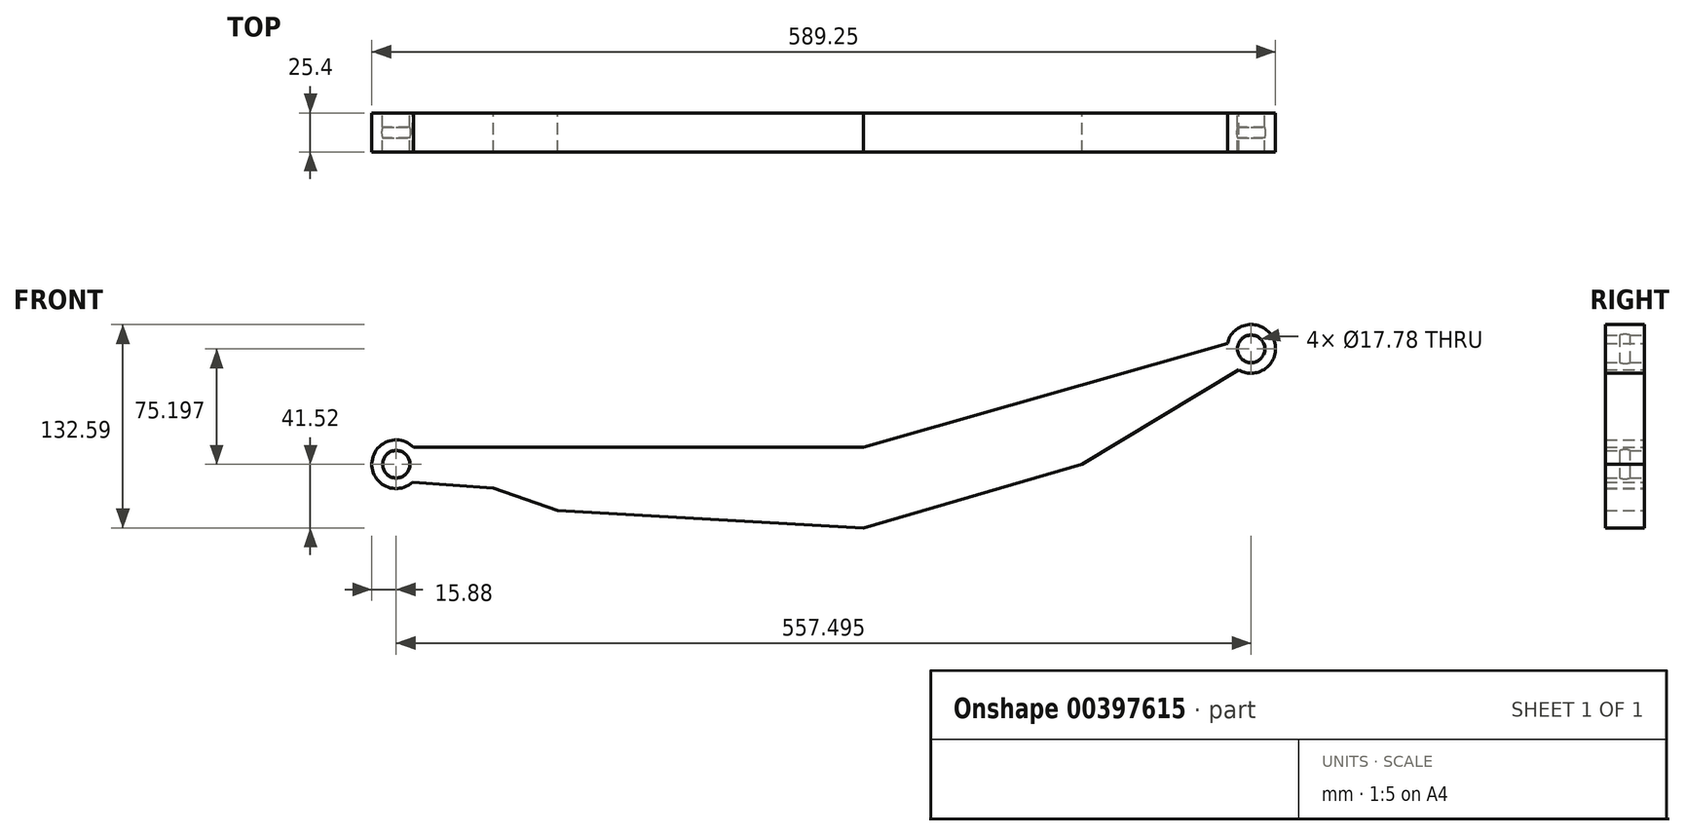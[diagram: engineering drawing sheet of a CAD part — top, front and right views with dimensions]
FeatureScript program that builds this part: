
annotation { "Feature Type Name" : "Feature", "Feature Type Description" : "" }
export const myFeature = defineFeature(function(context is Context, id is Id, definition is map)
    precondition{}
    {
        {
            var Q0;
            Q0=qCreatedBy(makeId("Front.planeOp"),FACE);
            var sketch = newSketch(context, id + "F0", { "sketchPlane" : qUnion([Q0])});
            skCircle(sketch, "E0", {"center": v(59.7, 0) * mm, "radius": 15.88 * mm});
            skLineSegment(sketch, "E1", {"start": v(59.7, 0) * mm, "end": v(59.7, 6.35) * mm});
            skLineSegment(sketch, "E2", {"start": v(59.7, 6.35) * mm, "end": v(59.7, 15.88) * mm});
            skLineSegment(sketch, "E3", {"start": v(59.7, 11.11) * mm, "end": v(364.5, 11.11) * mm});
            skLineSegment(sketch, "E4", {"start": v(59.7, 0) * mm, "end": v(59.7, -6.35) * mm});
            skLineSegment(sketch, "E5", {"start": v(59.7, -6.35) * mm, "end": v(59.7, -15.88) * mm});
            skLineSegment(sketch, "E6", {"start": v(59.7, -11.11) * mm, "end": v(123.05, -15.56) * mm});
            skLineSegment(sketch, "E7", {"start": v(123.05, -15.56) * mm, "end": v(164.98, -30.31) * mm});
            skLineSegment(sketch, "E8", {"start": v(164.98, -30.31) * mm, "end": v(364.5, -41.52) * mm});
            skLineSegment(sketch, "E9", {"start": v(364.5, -41.52) * mm, "end": v(364.5, 11.11) * mm});
            skLineSegment(sketch, "E10", {"start": v(614.5, 82.32) * mm, "end": v(619.92, 68.08) * mm});
            skCircle(sketch, "E11", {"center": v(617.2, 75.2) * mm, "radius": 15.88 * mm});
            skLineSegment(sketch, "E12", {"start": v(506.93, 0) * mm, "end": v(619.92, 68.08) * mm});
            skLineSegment(sketch, "E13", {"start": v(364.5, -41.52) * mm, "end": v(506.93, 0) * mm});
            skLineSegment(sketch, "E14", {"start": v(364.5, 11.11) * mm, "end": v(528.8, 57.91) * mm});
            skLineSegment(sketch, "E15", {"start": v(528.8, 57.91) * mm, "end": v(614.5, 82.32) * mm});
            skCircle(sketch, "E16", {"center": v(617.2, 75.2) * mm, "radius": 8.9 * mm});
            skCircle(sketch, "E17", {"center": v(59.7, 0) * mm, "radius": 8.9 * mm});
            skSolve(sketch);
        }
        {
            var Q0;
            {var subQ0=sQuery(id+"F0.wireOp",EDGE,"E3");var subQ3=sQuery(id+"F0.wireOp",EDGE,"E0");var subQ4=makeQuery(id+"F0.imprint","INTERSECT",VERTEX,{"derivedFrom":[subQ3,subQ0]});Q0=makeQuery(id+"F0.imprint","IMPRINT",FACE,{"disambiguationData":[TD([[makeQuery(id+"F0.imprint","IMPRINT",EDGE,{"disambiguationData":[TD([[subQ4,1.0]])],"derivedFrom":subQ3}),1.0]])]});}
            var Q1;
            {var subQ0=sQuery(id+"F0.wireOp",EDGE,"E2");var subQ1=sQuery(id+"F0.wireOp",EDGE,"E0");var subQ2=makeQuery(id+"F0.imprint","INTERSECT",VERTEX,{"derivedFrom":[subQ1,subQ0]});Q1=makeQuery(id+"F0.imprint","IMPRINT",FACE,{"disambiguationData":[TD([[makeQuery(id+"F0.imprint","IMPRINT",EDGE,{"disambiguationData":[TD([[subQ2,1.0]])],"derivedFrom":subQ1}),1.0]])]});}
            var Q2;
            {var subQ0=sQuery(id+"F0.wireOp",EDGE,"E2");var subQ4=sQuery(id+"F0.wireOp",EDGE,"E0");var subQ5=makeQuery(id+"F0.imprint","INTERSECT",VERTEX,{"derivedFrom":[subQ4,subQ0]});Q2=makeQuery(id+"F0.imprint","IMPRINT",FACE,{"disambiguationData":[TD([[makeQuery(id+"F0.imprint","IMPRINT",EDGE,{"disambiguationData":[TD([[subQ5,-1.0]])],"derivedFrom":subQ4}),1.0]])]});}
            var Q3;
            {var subQ0=sQuery(id+"F0.wireOp",EDGE,"E5");var subQ1=sQuery(id+"F0.wireOp",EDGE,"E0");var subQ2=makeQuery(id+"F0.imprint","INTERSECT",VERTEX,{"derivedFrom":[subQ1,subQ0]});Q3=makeQuery(id+"F0.imprint","IMPRINT",FACE,{"disambiguationData":[TD([[makeQuery(id+"F0.imprint","IMPRINT",EDGE,{"disambiguationData":[TD([[subQ2,-1.0]])],"derivedFrom":subQ1}),1.0]])]});}
            var Q4;
            {var subQ0=sQuery(id+"F0.wireOp",EDGE,"E7");Q4=makeQuery(id+"F0.imprint","IMPRINT",FACE,{"disambiguationData":[TD([[makeQuery(id+"F0.imprint","IMPRINT",EDGE,{"derivedFrom":subQ0}),1.0]])]});}
            var Q5;
            Q5=makeQuery(id+"F0.imprint","IMPRINT",FACE,{"disambiguationData":[TD([[makeQuery(id+"F0.imprint","IMPRINT",EDGE,{"derivedFrom":sQuery(id+"F0.wireOp",EDGE,"E9")}),-1.0]])]});
            var Q6;
            {var subQ0=sQuery(id+"F0.wireOp",EDGE,"E12");var subQ1=sQuery(id+"F0.wireOp",EDGE,"E11");var subQ2=makeQuery(id+"F0.imprint","INTERSECT",VERTEX,{"derivedFrom":[subQ1,subQ0]});Q6=makeQuery(id+"F0.imprint","IMPRINT",FACE,{"disambiguationData":[TD([[makeQuery(id+"F0.imprint","IMPRINT",EDGE,{"disambiguationData":[TD([[subQ2,1.0]])],"derivedFrom":subQ1}),1.0]])]});}
            var Q7;
            {var subQ0=sQuery(id+"F0.wireOp",EDGE,"E12");var subQ1=sQuery(id+"F0.wireOp",EDGE,"E11");var subQ2=makeQuery(id+"F0.imprint","INTERSECT",VERTEX,{"derivedFrom":[subQ1,subQ0]});Q7=makeQuery(id+"F0.imprint","IMPRINT",FACE,{"disambiguationData":[TD([[makeQuery(id+"F0.imprint","IMPRINT",EDGE,{"disambiguationData":[TD([[subQ2,-1.0]])],"derivedFrom":subQ1}),1.0]])]});}
            extrude(context, id + "F1", {"entities" : qUnion([Q0, Q1, Q2, Q3, Q4, Q5, Q6, Q7]), "depth" : 25.4 * mm});
        }
        {
            var Q0;
            Q0=makeQuery(id+"F1.opExtrude","CAP_FACE",FACE,{"disambiguationData":[OSD([sQuery(id+"F0.wireOp",EDGE,"E0"),sQuery(id+"F0.wireOp",EDGE,"E3"),sQuery(id+"F0.wireOp",EDGE,"E6"),sQuery(id+"F0.wireOp",EDGE,"E7"),sQuery(id+"F0.wireOp",EDGE,"E8"),sQuery(id+"F0.wireOp",EDGE,"E11"),sQuery(id+"F0.wireOp",EDGE,"E12"),sQuery(id+"F0.wireOp",EDGE,"E13"),sQuery(id+"F0.wireOp",EDGE,"E14"),sQuery(id+"F0.wireOp",EDGE,"E15"),sQuery(id+"F0.wireOp",EDGE,"E16"),sQuery(id+"F0.wireOp",EDGE,"E17")])],"isStart":false});
            cPlane(context, id + "F2", {"entities" : qUnion([Q0]), "cplaneType" : CPlaneType.OFFSET, "offset" : 12.7 * mm, "oppositeDirection" : true, "width" : 152.4 * mm, "height" : 152.4 * mm});
        }
        {
            var Q0;
            Q0=qCreatedBy(id+"F2.planeOp",FACE);
            var sketch = newSketch(context, id + "F3", { "sketchPlane" : qUnion([Q0])});
            skArc(sketch, "E18", {"start": v(59.7, -9.53) * mm, "mid": v(69.23, 0) * mm, "end": v(59.7, 9.53) * mm});
            skArc(sketch, "E19", {"start": v(617.2, 65.67) * mm, "mid": v(626.73, 75.2) * mm, "end": v(617.2, 84.72) * mm});
            skLineSegment(sketch, "E20", {"start": v(59.7, 0) * mm, "end": v(59.7, 9.53) * mm});
            skLineSegment(sketch, "E21", {"start": v(59.7, 9.53) * mm, "end": v(59.7, -9.53) * mm});
            skLineSegment(sketch, "E22", {"start": v(617.2, 75.2) * mm, "end": v(617.2, 84.72) * mm});
            skLineSegment(sketch, "E23", {"start": v(617.2, 84.72) * mm, "end": v(617.2, 65.67) * mm});
            skSolve(sketch);
        }
        {
            var Q0;
            {var subQ0=sQuery(id+"F3.wireOp",EDGE,"E18");Q0=makeQuery(id+"F3.imprint","IMPRINT",FACE,{"disambiguationData":[TD([[makeQuery(id+"F3.imprint","IMPRINT",EDGE,{"derivedFrom":subQ0}),1.0]])]});}
            var Q1;
            Q1=sQuery(id+"F3.wireOp",EDGE,"E21");
            revolve(context, id + "F4", {"operationType" : NewBodyOperationType.REMOVE, "entities" : qUnion([Q0]), "axis" : qUnion([Q1]), "revolveType" : RevolveType.FULL, "oppositeDirection" : true});
        }
        {
            var Q0;
            {var subQ0=sQuery(id+"F3.wireOp",EDGE,"E19");Q0=makeQuery(id+"F3.imprint","IMPRINT",FACE,{"disambiguationData":[TD([[makeQuery(id+"F3.imprint","IMPRINT",EDGE,{"derivedFrom":subQ0}),1.0]])]});}
            var Q1;
            Q1=sQuery(id+"F3.wireOp",EDGE,"E23");
            revolve(context, id + "F5", {"operationType" : NewBodyOperationType.REMOVE, "entities" : qUnion([Q0]), "axis" : qUnion([Q1]), "revolveType" : RevolveType.FULL, "oppositeDirection" : true});
        }
    });
